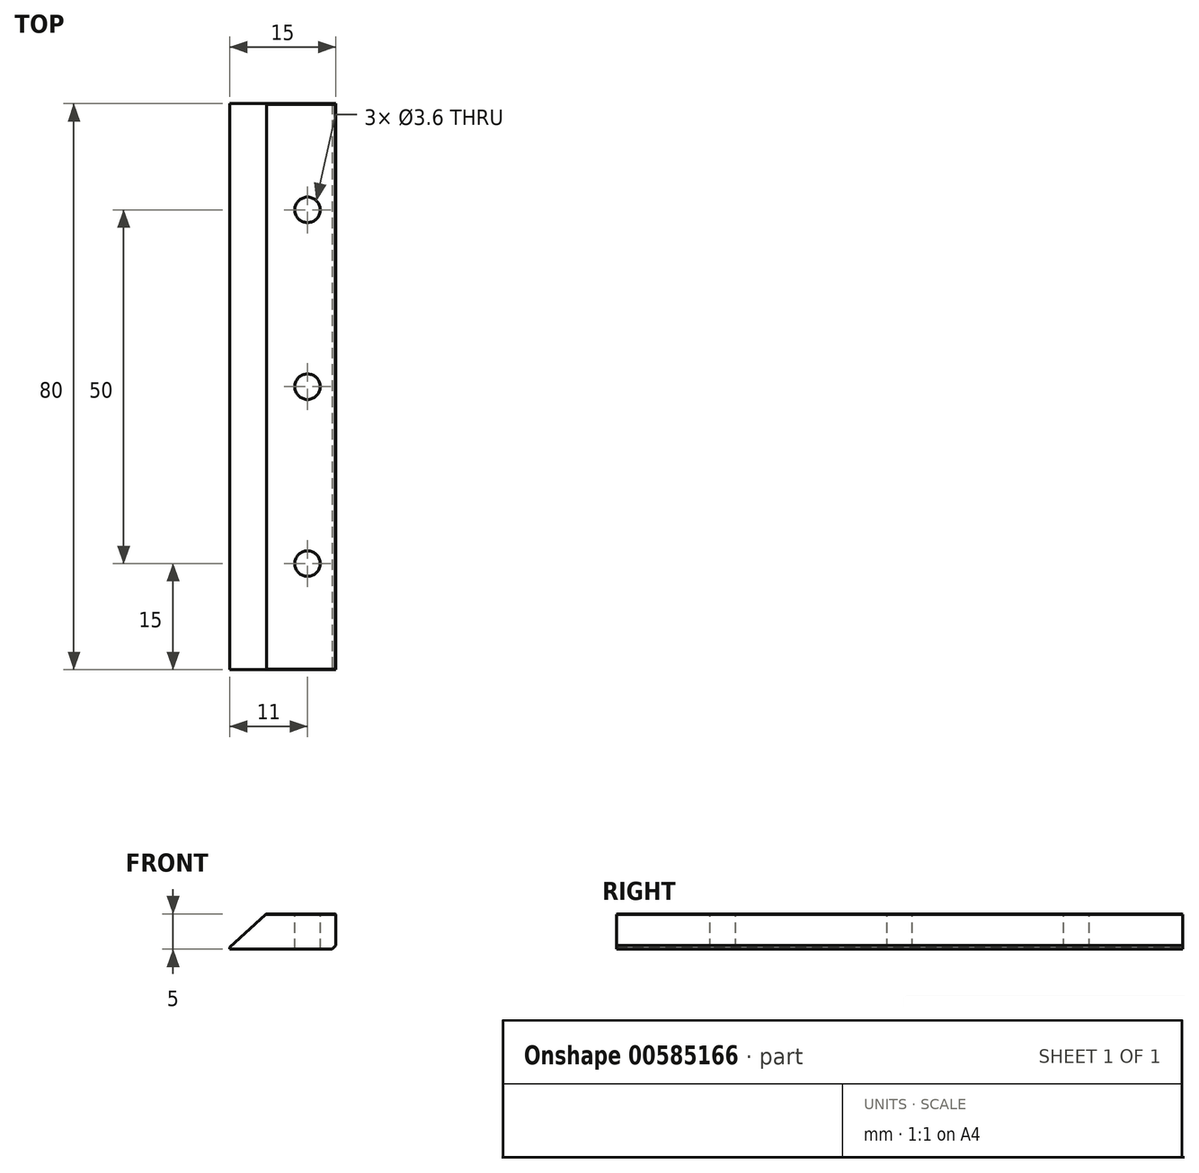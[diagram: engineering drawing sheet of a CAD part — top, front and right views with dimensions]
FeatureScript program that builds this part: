
annotation { "Feature Type Name" : "Feature", "Feature Type Description" : "" }
export const myFeature = defineFeature(function(context is Context, id is Id, definition is map)
    precondition{}
    {
        {
            var Q0;
            Q0=qCreatedBy(makeId("Front.planeOp"),FACE);
            var sketch = newSketch(context, id + "F0", { "sketchPlane" : qUnion([Q0])});
            skLineSegment(sketch, "E0.bottom", {"start": v(0, 0) * mm, "end": v(15, 0) * mm});
            skLineSegment(sketch, "E0.top", {"start": v(5.22, 5) * mm, "end": v(15, 5) * mm});
            skLineSegment(sketch, "E0.left", {"start": v(0, 0) * mm, "end": v(0, 0.3) * mm});
            skLineSegment(sketch, "E0.right", {"start": v(15, 0) * mm, "end": v(15, 5) * mm});
            skLineSegment(sketch, "E1", {"start": v(0, 0.3) * mm, "end": v(5.22, 5) * mm});
            skSolve(sketch);
        }
        {
            var Q0;
            Q0 = qSketchRegion(id + "F0", true);
            extrude(context, id + "F1", {"entities" : qUnion([Q0]), "depth" : 80 * mm, "offsetDistance" : 25 * mm});
        }
        {
            var Q0;
            Q0=makeQuery(id+"F1.opExtrude","SWEPT_FACE",FACE,{"disambiguationData":[OSD([sQuery(id+"F0.wireOp",EDGE,"E0.top")])]});
            var sketch = newSketch(context, id + "F2", { "sketchPlane" : qUnion([Q0])});
            skLineSegment(sketch, "E2", {"start": v(5.22, -40) * mm, "end": v(15, -40) * mm, "construction": true});
            skCircle(sketch, "E3", {"center": v(11, -40) * mm, "radius": 1.8 * mm});
            skCircle(sketch, "E4", {"center": v(11, -15) * mm, "radius": 1.8 * mm});
            skCircle(sketch, "E5", {"center": v(11, -65) * mm, "radius": 1.8 * mm});
            skSolve(sketch);
        }
        {
            var Q0;
            Q0 = qSketchRegion(id + "F2", true);
            extrude(context, id + "F3", {"entities" : qUnion([Q0]), "operationType" : NewBodyOperationType.REMOVE, "endBound" : BoundingType.THROUGH_ALL, "oppositeDirection" : true, "depth" : 25 * mm, "offsetDistance" : 25 * mm});
        }
        {
            var Q0;
            Q0=makeQuery(id+"F1.opExtrude","SWEPT_EDGE",EDGE,{"disambiguationData":[OSD([sQuery(id+"F0.wireOp",EDGE,"E0.bottom"),sQuery(id+"F0.wireOp",EDGE,"E0.right")])]});
            chamfer(context, id + "F4", {"entities" : qUnion([Q0]), "width" : 0.5 * mm, "tangentPropagation" : true});
        }
        {
            var Q0;
            Q0=makeQuery(id+"F1.opExtrude","SWEPT_EDGE",EDGE,{"disambiguationData":[OSD([sQuery(id+"F0.wireOp",EDGE,"E0.top"),sQuery(id+"F0.wireOp",EDGE,"E0.right")])]});
            var Q1;
            Q1=makeQuery(id+"F1.opExtrude","CAP_EDGE",EDGE,{"disambiguationData":[OSD([sQuery(id+"F0.wireOp",EDGE,"E0.top")])],"isStart":false});
            var Q2;
            Q2=makeQuery(id+"F1.opExtrude","CAP_EDGE",EDGE,{"disambiguationData":[OSD([sQuery(id+"F0.wireOp",EDGE,"E0.top")])],"isStart":true});
            chamfer(context, id + "F5", {"entities" : qUnion([Q0, Q1, Q2]), "width" : 0.1 * mm, "tangentPropagation" : true});
        }
    });
